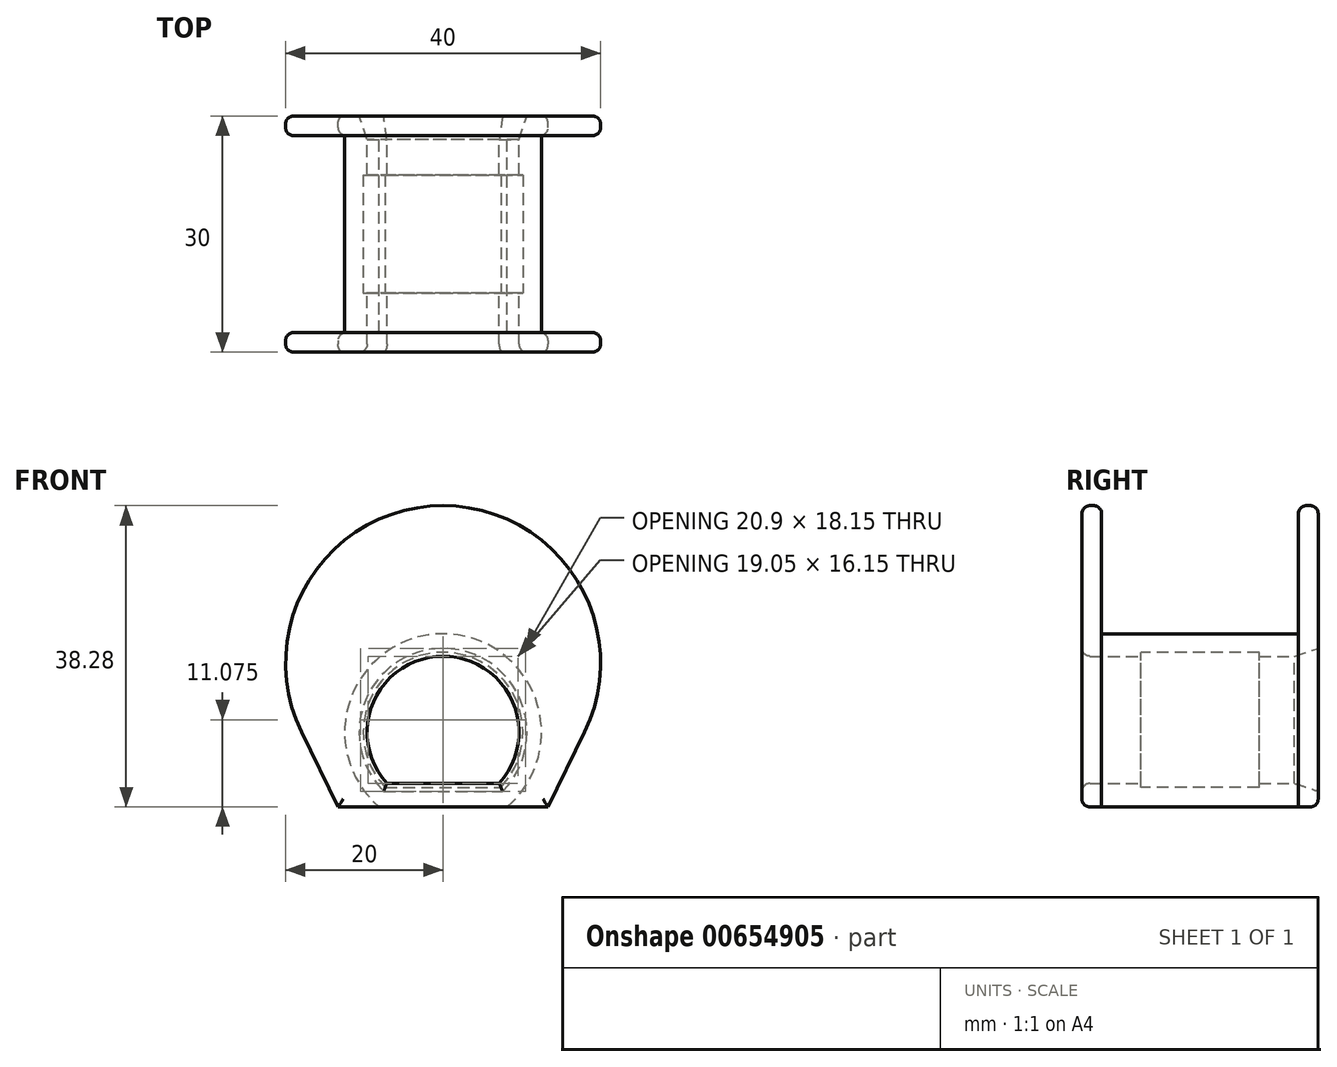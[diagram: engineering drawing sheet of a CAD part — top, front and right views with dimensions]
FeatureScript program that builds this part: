
annotation { "Feature Type Name" : "Feature", "Feature Type Description" : "" }
export const myFeature = defineFeature(function(context is Context, id is Id, definition is map)
    precondition{}
    {
        {
            var Q0;
            Q0=qCreatedBy(makeId("Front.planeOp"),FACE);
            var sketch = newSketch(context, id + "F0", { "sketchPlane" : qUnion([Q0])});
            skArc(sketch, "E0", {"start": v(7.13, -6.5) * mm, "mid": v(0, 9.65) * mm, "end": v(-7.13, -6.5) * mm});
            skArc(sketch, "E1", {"start": v(8.12, -9.5) * mm, "mid": v(0, 12.5) * mm, "end": v(-8.12, -9.5) * mm});
            skLineSegment(sketch, "E2", {"start": v(-12.5, 0) * mm, "end": v(12.5, 0) * mm, "construction": true});
            skLineSegment(sketch, "E3", {"start": v(0, 12.5) * mm, "end": v(0, -9.5) * mm, "construction": true});
            skLineSegment(sketch, "E4", {"start": v(-7.13, -6.5) * mm, "end": v(7.13, -6.5) * mm});
            skLineSegment(sketch, "E5.0", {"start": v(-13.33, -9.5) * mm, "end": v(13.33, -9.5) * mm});
            skArc(sketch, "E6", {"start": v(17.97, 0) * mm, "mid": v(0, 28.78) * mm, "end": v(-17.97, 0) * mm});
            skLineSegment(sketch, "E7", {"start": v(17.97, 0) * mm, "end": v(13.33, -9.5) * mm});
            skLineSegment(sketch, "E8", {"start": v(-17.97, 0) * mm, "end": v(-13.33, -9.5) * mm});
            skSolve(sketch);
        }
        {
            var Q0;
            Q0=makeQuery(id+"F0.imprint","IMPRINT",FACE,{"disambiguationData":[TD([[makeQuery(id+"F0.imprint","IMPRINT",EDGE,{"derivedFrom":sQuery(id+"F0.wireOp",EDGE,"E0")}),-1.0]])]});
            extrude(context, id + "F1", {"entities" : qUnion([Q0]), "depth" : 30 * mm, "offsetDistance" : 25 * mm});
        }
        {
            var Q0;
            Q0=makeQuery(id+"F0.imprint","IMPRINT",FACE,{"disambiguationData":[TD([[makeQuery(id+"F0.imprint","IMPRINT",EDGE,{"derivedFrom":sQuery(id+"F0.wireOp",EDGE,"E1")}),-1.0]])]});
            extrude(context, id + "F2", {"entities" : qUnion([Q0]), "operationType" : NewBodyOperationType.ADD, "depth" : 2.5 * mm, "offsetDistance" : 25 * mm});
        }
        {
            var Q0;
            Q0=makeQuery(id+"F1.opExtrude","CAP_FACE",FACE,{"disambiguationData":[OSD([sQuery(id+"F0.wireOp",EDGE,"E0"),sQuery(id+"F0.wireOp",EDGE,"E1"),sQuery(id+"F0.wireOp",EDGE,"E4"),sQuery(id+"F0.wireOp",EDGE,"E5.0")])],"isStart":false});
            var sketch = newSketch(context, id + "F3", { "sketchPlane" : qUnion([Q0])});
            skArc(sketch, "E9.0", {"start": v(17.97, 0) * mm, "mid": v(0, 28.78) * mm, "end": v(-17.97, 0) * mm});
            skArc(sketch, "E9.1", {"start": v(8.12, -9.5) * mm, "mid": v(0, 12.5) * mm, "end": v(-8.12, -9.5) * mm});
            skLineSegment(sketch, "E10.0", {"start": v(17.97, 0) * mm, "end": v(13.33, -9.5) * mm});
            skLineSegment(sketch, "E10.1", {"start": v(-13.33, -9.5) * mm, "end": v(-8.12, -9.5) * mm});
            skLineSegment(sketch, "E10.2", {"start": v(-17.97, 0) * mm, "end": v(-13.33, -9.5) * mm});
            skLineSegment(sketch, "E11.trimOffspring", {"start": v(8.12, -9.5) * mm, "end": v(13.33, -9.5) * mm});
            skSolve(sketch);
        }
        {
            var Q0;
            Q0 = qSketchRegion(id + "F3", true);
            extrude(context, id + "F4", {"entities" : qUnion([Q0]), "operationType" : NewBodyOperationType.ADD, "oppositeDirection" : true, "depth" : 2.5 * mm, "offsetDistance" : 25 * mm});
        }
        {
            var Q0;
            Q0=makeQuery(id+"F1.opExtrude","CAP_EDGE",EDGE,{"disambiguationData":[OSD([sQuery(id+"F0.wireOp",EDGE,"E0")])],"isStart":true});
            var Q1;
            Q1=makeQuery(id+"F1.opExtrude","CAP_EDGE",EDGE,{"disambiguationData":[OSD([sQuery(id+"F0.wireOp",EDGE,"E4")])],"isStart":true});
            chamfer(context, id + "F5", {"entities" : qUnion([Q0, Q1]), "chamferType" : ChamferType.TWO_OFFSETS, "width1" : 1 * mm, "oppositeDirection" : false, "width2" : 3 * mm, "tangentPropagation" : true});
        }
        {
            var Q0;
            Q0=makeQuery(id+"F2.opExtrude","CAP_EDGE",EDGE,{"disambiguationData":[OSD([sQuery(id+"F0.wireOp",EDGE,"E1")])],"isStart":false});
            var Q1;
            Q1=makeQuery(id+"F4.opExtrude","CAP_EDGE",EDGE,{"disambiguationData":[OSD([sQuery(id+"F3.wireOp",EDGE,"E9.1")])],"isStart":false});
            var Q2;
            Q2=makeQuery(id+"F2.opExtrude","CAP_EDGE",EDGE,{"disambiguationData":[OSD([sQuery(id+"F0.wireOp",EDGE,"E6")])],"isStart":true});
            var Q3;
            Q3=makeQuery(id+"F4.opExtrude","CAP_EDGE",EDGE,{"disambiguationData":[OSD([sQuery(id+"F3.wireOp",EDGE,"E9.0")])],"isStart":true});
            var Q4;
            Q4=makeQuery(id+"F1.opExtrude","CAP_EDGE",EDGE,{"disambiguationData":[OSD([sQuery(id+"F0.wireOp",EDGE,"E5.0")])],"isStart":true});
            var Q5;
            Q5=makeQuery(id+"F1.opExtrude","CAP_EDGE",EDGE,{"disambiguationData":[OSD([sQuery(id+"F0.wireOp",EDGE,"E5.0")])],"isStart":false});
            var Q6;
            Q6=makeQuery(id+"F1.opExtrude","CAP_EDGE",EDGE,{"disambiguationData":[OSD([sQuery(id+"F0.wireOp",EDGE,"E0")])],"isStart":false});
            var Q7;
            Q7=makeQuery(id+"F1.opExtrude","CAP_EDGE",EDGE,{"disambiguationData":[OSD([sQuery(id+"F0.wireOp",EDGE,"E4")])],"isStart":false});
            fillet(context, id + "F6", {"entities" : qUnion([Q0, Q1, Q2, Q3, Q4, Q5, Q6, Q7]), "radius" : 1 * mm, "tangentPropagation" : true, "allowEdgeOverflow" : false});
        }
        {
            var Q0;
            Q0=makeQuery(id+"F4.opExtrude","CAP_EDGE",EDGE,{"disambiguationData":[OSD([sQuery(id+"F3.wireOp",EDGE,"E9.0")])],"isStart":false});
            var Q1;
            Q1=makeQuery(id+"F2.opExtrude","CAP_EDGE",EDGE,{"disambiguationData":[OSD([sQuery(id+"F0.wireOp",EDGE,"E6")])],"isStart":false});
            fillet(context, id + "F7", {"entities" : qUnion([Q0, Q1]), "radius" : 1 * mm, "tangentPropagation" : true, "allowEdgeOverflow" : false});
        }
        {
            var Q0;
            Q0=qCreatedBy(makeId("Front.planeOp"),FACE);
            cPlane(context, id + "F8", {"entities" : qUnion([Q0]), "cplaneType" : CPlaneType.OFFSET, "offset" : 15 * mm, "width" : 150 * mm, "height" : 150 * mm});
        }
        {
            var Q0;
            Q0=qCreatedBy(id+"F8.planeOp",FACE);
            var sketch = newSketch(context, id + "F9", { "sketchPlane" : qUnion([Q0])});
            skArc(sketch, "E12.0", {"start": v(7.13, -6.5) * mm, "mid": v(0, 9.65) * mm, "end": v(-7.13, -6.5) * mm});
            skLineSegment(sketch, "E12.1", {"start": v(-7.13, -6.5) * mm, "end": v(7.13, -6.5) * mm});
            skLineSegment(sketch, "E13.0", {"start": v(-7.35, -7) * mm, "end": v(7.35, -7) * mm});
            skArc(sketch, "E13.1", {"start": v(7.35, -7) * mm, "mid": v(0, 10.15) * mm, "end": v(-7.35, -7) * mm});
            skSolve(sketch);
        }
        {
            var Q0;
            Q0 = qSketchRegion(id + "F9", true);
            extrude(context, id + "F10", {"entities" : qUnion([Q0]), "operationType" : NewBodyOperationType.REMOVE, "endBound" : BoundingType.SYMMETRIC, "oppositeDirection" : true, "depth" : 15 * mm, "offsetDistance" : 25 * mm});
        }
    });
